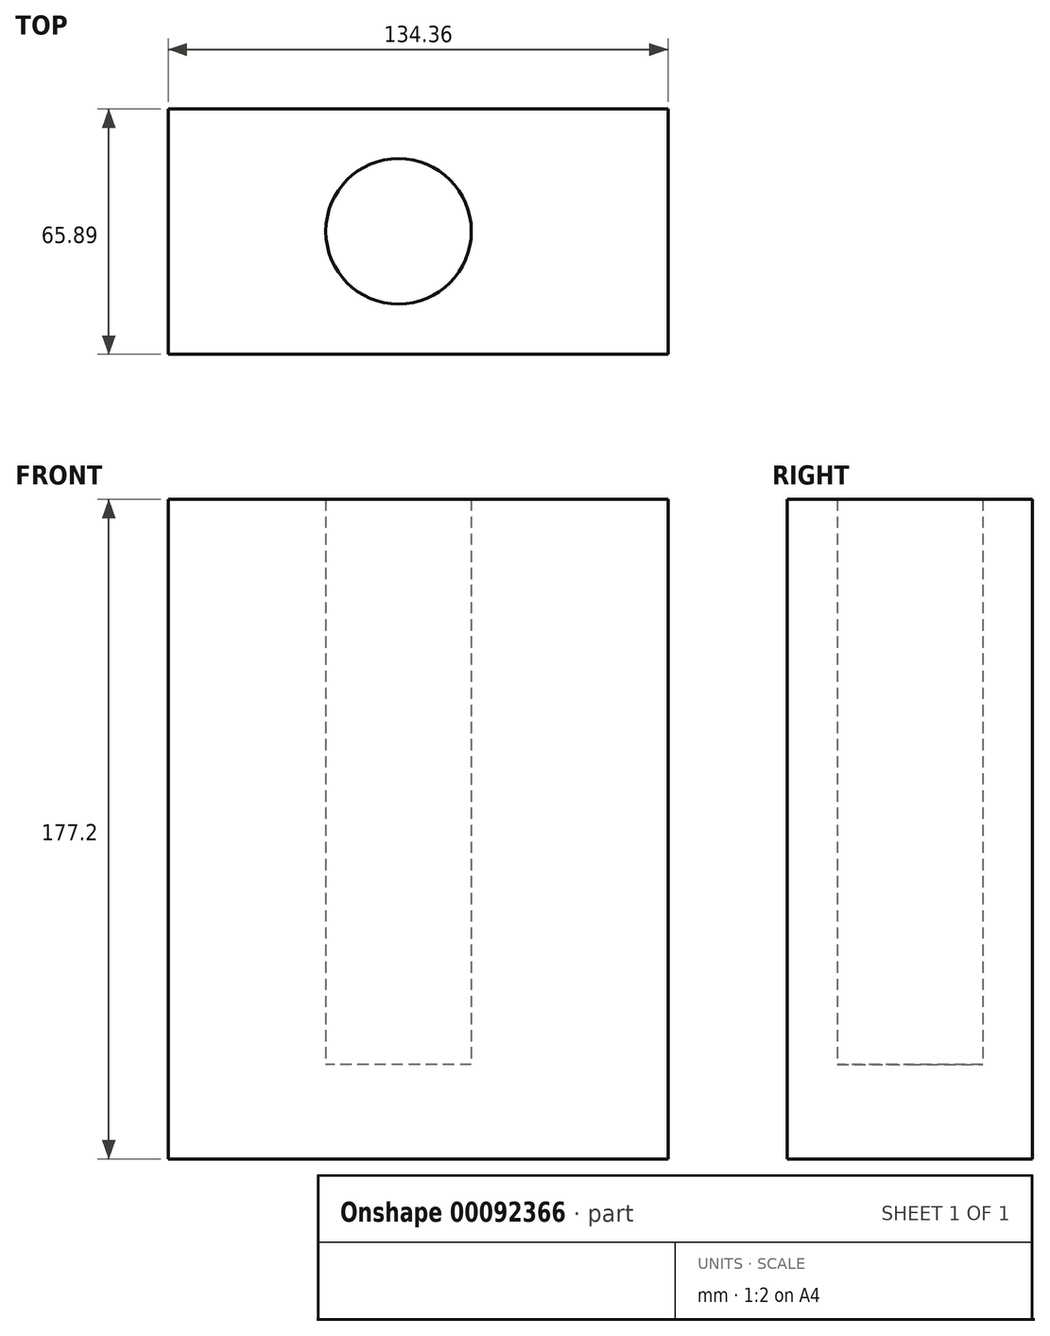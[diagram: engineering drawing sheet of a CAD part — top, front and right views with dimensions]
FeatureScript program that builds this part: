
annotation { "Feature Type Name" : "Feature", "Feature Type Description" : "" }
export const myFeature = defineFeature(function(context is Context, id is Id, definition is map)
    precondition{}
    {
        {
            var Q0;
            Q0=qCreatedBy(makeId("Top.planeOp"),FACE);
            var sketch = newSketch(context, id + "F0", { "sketchPlane" : qUnion([Q0])});
            skLineSegment(sketch, "E0.bottom", {"start": v(-67.32, -26.67) * mm, "end": v(67.04, -26.67) * mm});
            skLineSegment(sketch, "E0.top", {"start": v(-67.32, 39.22) * mm, "end": v(67.04, 39.22) * mm});
            skLineSegment(sketch, "E0.left", {"start": v(-67.32, -26.67) * mm, "end": v(-67.32, 39.22) * mm});
            skLineSegment(sketch, "E0.right", {"start": v(67.04, -26.67) * mm, "end": v(67.04, 39.22) * mm});
            skSolve(sketch);
        }
        {
            var Q0;
            Q0=makeQuery(id+"F0.imprint","IMPRINT",FACE,{"disambiguationData":[TD([[makeQuery(id+"F0.imprint","IMPRINT",EDGE,{"derivedFrom":sQuery(id+"F0.wireOp",EDGE,"E0.bottom")}),1.0]])]});
            extrude(context, id + "F1", {"entities" : qUnion([Q0]), "endBound" : BoundingType.SYMMETRIC, "depth" : 25.4 * mm});
        }
        {
            var Q0;
            Q0=makeQuery(id+"F1.opExtrude","CAP_FACE",FACE,{"disambiguationData":[OSD([sQuery(id+"F0.wireOp",EDGE,"E0.bottom"),sQuery(id+"F0.wireOp",EDGE,"E0.top"),sQuery(id+"F0.wireOp",EDGE,"E0.left"),sQuery(id+"F0.wireOp",EDGE,"E0.right")])],"isStart":false});
            var sketch = newSketch(context, id + "F2", { "sketchPlane" : qUnion([Q0])});
            skCircle(sketch, "E1", {"center": v(-5.4, 6.39) * mm, "radius": 19.56 * mm});
            skSolve(sketch);
        }
        {
            var Q0;
            Q0=makeQuery(id+"F2.imprint","IMPRINT",FACE,{"disambiguationData":[TD([[makeQuery(id+"F2.imprint","IMPRINT",EDGE,{"derivedFrom":sQuery(id+"F2.wireOp",EDGE,"E1")}),-1.0]])]});
            extrude(context, id + "F3", {"entities" : qUnion([Q0]), "operationType" : NewBodyOperationType.ADD, "endBound" : BoundingType.THROUGH_ALL, "depth" : 25.4 * mm});
        }
    });
